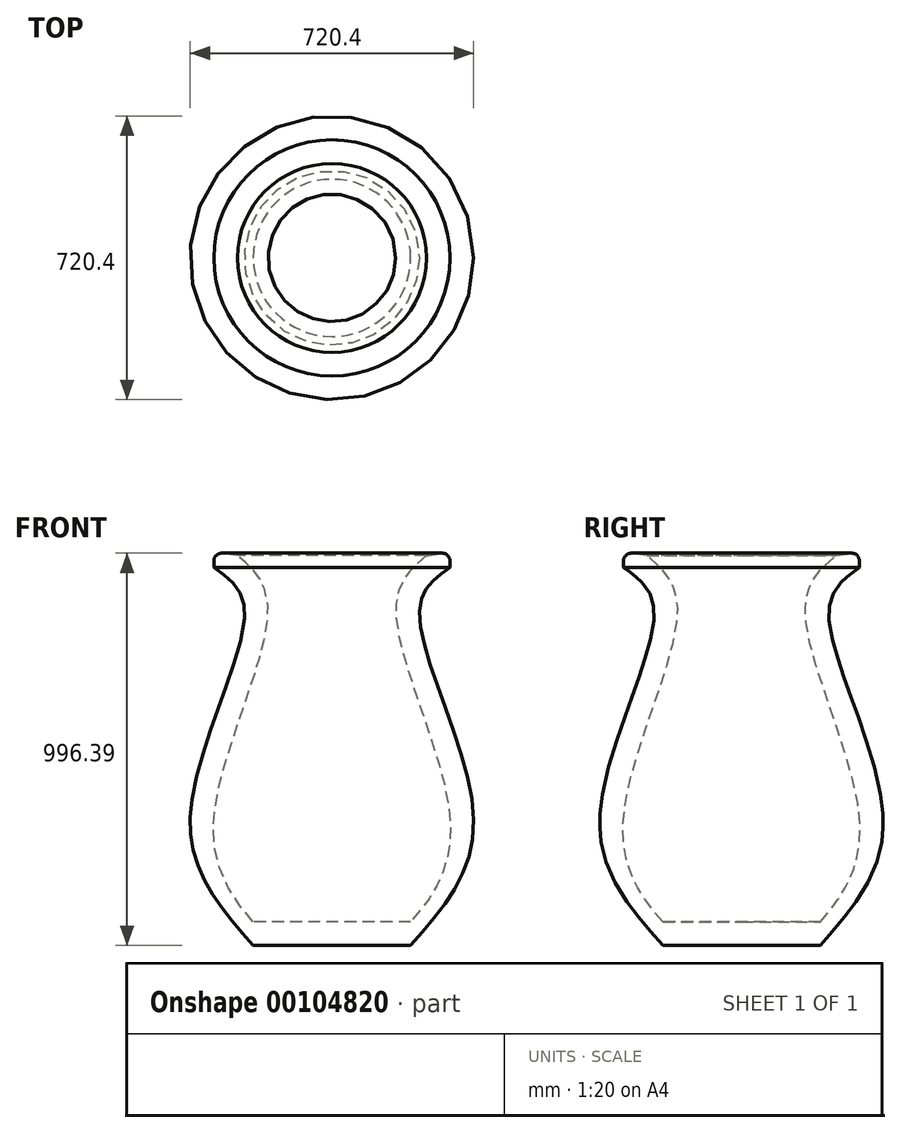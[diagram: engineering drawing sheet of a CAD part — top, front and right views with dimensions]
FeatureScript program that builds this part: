
annotation { "Feature Type Name" : "Feature", "Feature Type Description" : "" }
export const myFeature = defineFeature(function(context is Context, id is Id, definition is map)
    precondition{}
    {
        {
            var Q0;
            Q0=qCreatedBy(makeId("Front.planeOp"),FACE);
            var sketch = newSketch(context, id + "F0", { "sketchPlane" : qUnion([Q0])});
            skLineSegment(sketch, "E0", {"start": v(0, 476.8) * mm, "end": v(0, -523.2) * mm, "construction": true});
            skPoint(sketch, "E1", {"position": v(0, 466.8) * mm});
            skLineSegment(sketch, "E2", {"start": v(-300, 476.8) * mm, "end": v(-300, 436.8) * mm});
            skFitSpline(sketch, "E3", {"points": [v(-240, 466.8) * mm, v(-161.97, 326.5) * mm, v(-300, -198.95) * mm, v(-200, -463.2) * mm], "startDerivative": vector(545, -433.37) * mm, "endDerivative": vector(593.95, -663.85) * mm});
            skPoint(sketch, "E4", {"position": v(0, -523.2) * mm});
            skPoint(sketch, "E5", {"position": v(-200, -523.2) * mm});
            skPoint(sketch, "E6", {"position": v(-360, -198.95) * mm});
            skPoint(sketch, "E7", {"position": v(-221.97, 326.5) * mm});
            skFitSpline(sketch, "E8", {"points": [v(-300, 436.8) * mm, v(-221.97, 326.5) * mm, v(-360, -198.95) * mm, v(-200, -523.2) * mm], "startDerivative": vector(526.05, -367.93) * mm, "endDerivative": vector(701.5, -788.5) * mm});
            skLineSegment(sketch, "E9", {"start": v(-200, -463.2) * mm, "end": v(0, -463.2) * mm});
            skLineSegment(sketch, "E10", {"start": v(-200, -523.2) * mm, "end": v(0, -523.2) * mm});
            skLineSegment(sketch, "E11", {"start": v(0, 476.8) * mm, "end": v(0, -523.2) * mm});
            skLineSegment(sketch, "E12", {"start": v(-240, 466.8) * mm, "end": v(-300, 476.8) * mm});
            skLineSegment(sketch, "E13", {"start": v(-300, 476.8) * mm, "end": v(0, 476.8) * mm, "construction": true});
            skSolve(sketch);
        }
        {
            var Q0;
            Q0 = qSketchRegion(id + "F0", true);
            var Q1;
            Q1=sQuery(id+"F0.wireOp",EDGE,"E11");
            var Q2;
            Q2=sQuery(id+"F0.wireOp",EDGE,"E11");
            revolve(context, id + "F1", {"entities" : qUnion([Q0]), "surfaceEntities" : qUnion([Q1]), "axis" : qUnion([Q2]), "revolveType" : RevolveType.TWO_DIRECTIONS, "angle" : 330 * degree, "angleBack" : 330 * degree});
        }
        {
            var Q0;
            Q0=makeQuery(id+"F1.opRevolve","SWEPT_EDGE",EDGE,{"disambiguationData":[OSD([sQuery(id+"F0.wireOp",EDGE,"E2"),sQuery(id+"F0.wireOp",EDGE,"E12")])]});
            fillet(context, id + "F2", {"entities" : qUnion([Q0]), "radius" : 20 * mm, "tangentPropagation" : true, "allowEdgeOverflow" : false});
        }
    });
